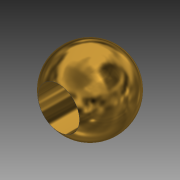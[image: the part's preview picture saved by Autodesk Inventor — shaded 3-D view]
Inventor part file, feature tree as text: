
AUTODESK INVENTOR PART (.ipt)
format: ipt  version: 2014 SP1 (Build 180222100, 222)  size: 118,272 bytes
history: native  units: in
note: dims shown in document units (in); Inventor stores cm internally (conversion verified against a paired STEP export)
features: sketch x2, revolve x1, extrude x1
ambient origin geometry x8: Origin, YZ Plane, XZ Plane, XY Plane, X Axis, Y Axis, Z Axis, Center Point
bodies: Solid1 (feature_tree)
feature tree (4):
  revolve  "Revolution1"  Angle=90.0deg
  extrude  "Extrusion1"  Depth=0.3937in TaperAngle=0.0deg
  sketch  "Sketch1"  dims[d0=0.2492in d1=90.0deg]
  sketch  "Sketch2"  dims[d2=0.1378in d3=0.3937in d4=0.0in]
